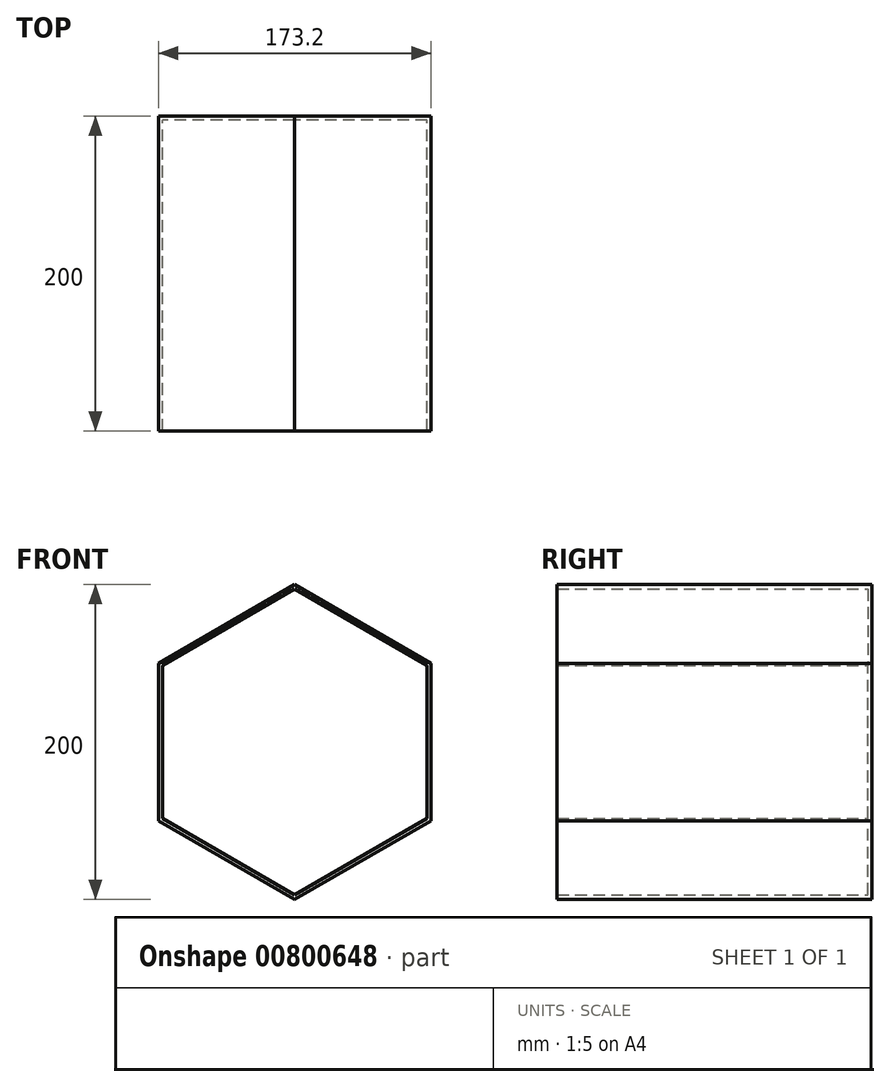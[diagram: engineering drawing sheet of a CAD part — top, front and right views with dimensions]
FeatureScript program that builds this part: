
annotation { "Feature Type Name" : "Feature", "Feature Type Description" : "" }
export const myFeature = defineFeature(function(context is Context, id is Id, definition is map)
    precondition{}
    {
        {
            var Q0;
            Q0=qCreatedBy(makeId("Front.planeOp"),FACE);
            var sketch = newSketch(context, id + "F0", { "sketchPlane" : qUnion([Q0])});
            skCircle(sketch, "E0.cCircle", {"center": v(0, 0) * mm, "radius": 86.6 * mm, "construction": true});
            skLineSegment(sketch, "E0.0", {"start": v(-86.6, -50) * mm, "end": v(-86.6, 50) * mm});
            skLineSegment(sketch, "E0.1", {"start": v(-86.6, 50) * mm, "end": v(0, 100) * mm});
            skLineSegment(sketch, "E0.2", {"start": v(0, 100) * mm, "end": v(86.6, 50) * mm});
            skLineSegment(sketch, "E0.3", {"start": v(86.6, 50) * mm, "end": v(86.6, -50) * mm});
            skLineSegment(sketch, "E0.4", {"start": v(86.6, -50) * mm, "end": v(0, -100) * mm});
            skLineSegment(sketch, "E0.5", {"start": v(0, -100) * mm, "end": v(-86.6, -50) * mm});
            skPoint(sketch, "E0.0.midPoint", {"position": v(-86.6, 0) * mm});
            skSolve(sketch);
        }
        {
            var Q0;
            Q0=makeQuery(id+"F0.imprint","IMPRINT",FACE,{"disambiguationData":[TD([[makeQuery(id+"F0.imprint","IMPRINT",EDGE,{"derivedFrom":sQuery(id+"F0.wireOp",EDGE,"E0.0")}),-1.0]])]});
            extrude(context, id + "F1", {"entities" : qUnion([Q0]), "depth" : 200 * mm, "offsetDistance" : 25 * mm});
        }
        {
            var Q0;
            Q0=makeQuery(id+"F1.opExtrude","CAP_FACE",FACE,{"disambiguationData":[OSD([sQuery(id+"F0.wireOp",EDGE,"E0.0"),sQuery(id+"F0.wireOp",EDGE,"E0.1"),sQuery(id+"F0.wireOp",EDGE,"E0.2"),sQuery(id+"F0.wireOp",EDGE,"E0.3"),sQuery(id+"F0.wireOp",EDGE,"E0.4"),sQuery(id+"F0.wireOp",EDGE,"E0.5")])],"isStart":false});
            shell(context, id + "F2", {"entities" : qUnion([Q0]), "thickness" : 2.5 * mm});
        }
    });
